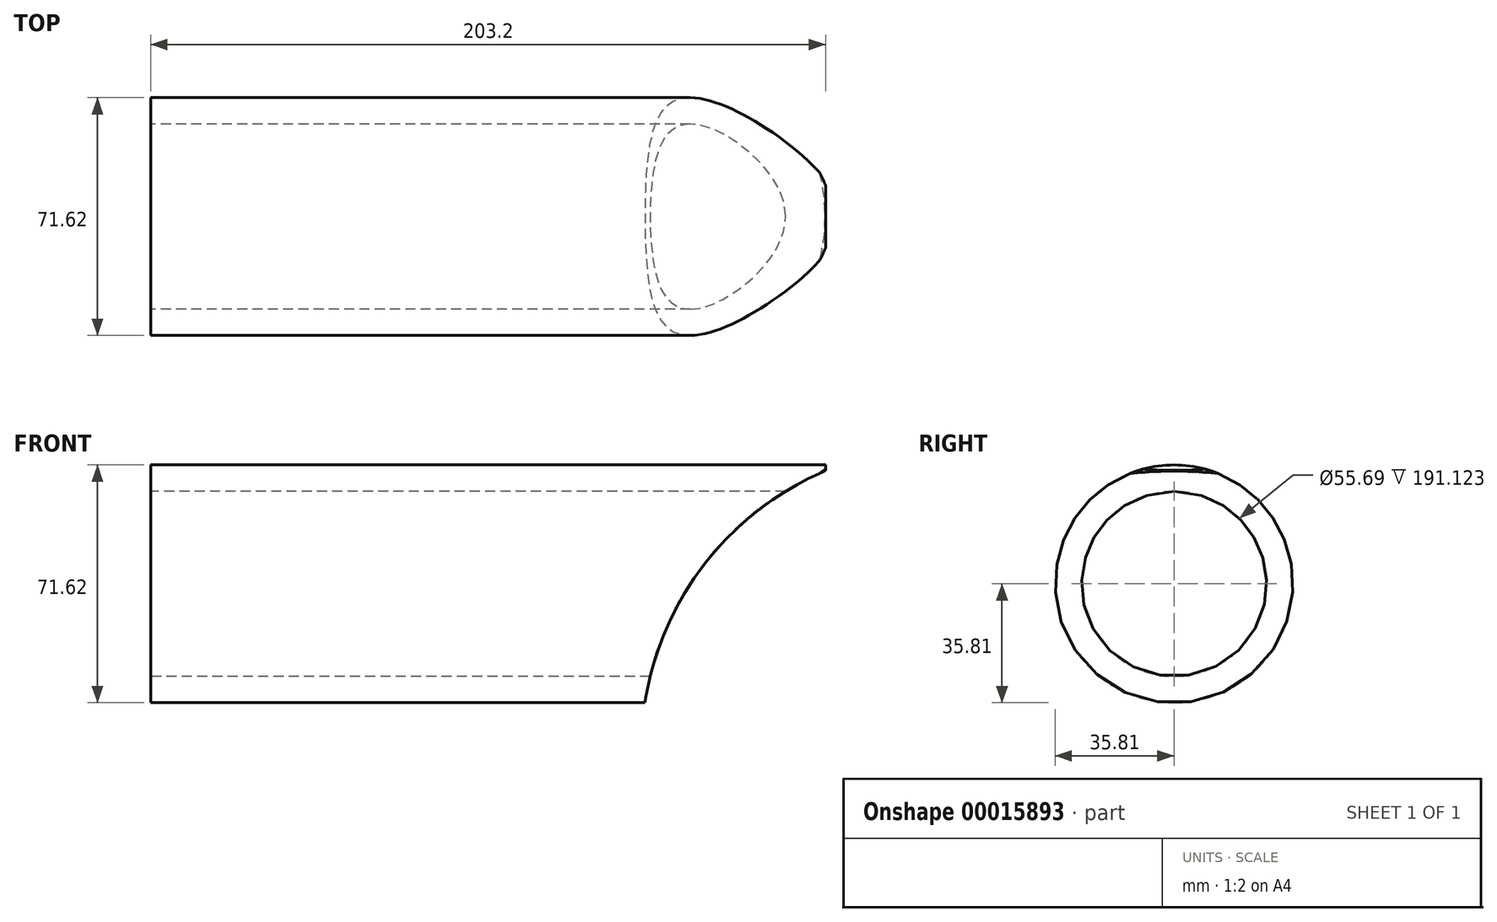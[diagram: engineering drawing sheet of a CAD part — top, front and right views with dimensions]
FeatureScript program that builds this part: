
annotation { "Feature Type Name" : "Feature", "Feature Type Description" : "" }
export const myFeature = defineFeature(function(context is Context, id is Id, definition is map)
    precondition{}
    {
        {
            var Q0;
            Q0=qCreatedBy(makeId("Right.planeOp"),FACE);
            var sketch = newSketch(context, id + "F0", { "sketchPlane" : qUnion([Q0])});
            skCircle(sketch, "E0", {"center": v(0, 0) * mm, "radius": 27.84 * mm});
            skCircle(sketch, "E1", {"center": v(0, 0) * mm, "radius": 35.81 * mm});
            skSolve(sketch);
        }
        {
            var Q0;
            Q0=makeQuery(id+"F0.imprint","IMPRINT",FACE,{"disambiguationData":[TD([[makeQuery(id+"F0.imprint","IMPRINT",EDGE,{"derivedFrom":sQuery(id+"F0.wireOp",EDGE,"E0")}),-1.0]])]});
            extrude(context, id + "F1", {"entities" : qUnion([Q0]), "depth" : 203.2 * mm});
        }
        {
            var Q0;
            Q0=qCreatedBy(makeId("Front.planeOp"),FACE);
            var sketch = newSketch(context, id + "F2", { "sketchPlane" : qUnion([Q0])});
            skCircle(sketch, "E2", {"center": v(238.57, -49.56) * mm, "radius": 90.78 * mm});
            skSolve(sketch);
        }
        {
            var Q0;
            Q0=makeQuery(id+"F2.imprint","IMPRINT",FACE,{"disambiguationData":[TD([[makeQuery(id+"F2.imprint","IMPRINT",EDGE,{"derivedFrom":sQuery(id+"F2.wireOp",EDGE,"E2")}),1.0]])]});
            extrude(context, id + "F3", {"entities" : qUnion([Q0]), "operationType" : NewBodyOperationType.REMOVE, "endBound" : BoundingType.THROUGH_ALL, "oppositeDirection" : true, "depth" : 25.4 * mm, "hasSecondDirection" : true, "secondDirectionBound" : SecondDirectionBoundingType.THROUGH_ALL, "secondDirectionOppositeDirection" : false, "secondDirectionDepth" : 25.4 * mm});
        }
        {
            var Q0;
            Q0=qCreatedBy(makeId("Top.planeOp"),FACE);
            var sketch = newSketch(context, id + "F4", { "sketchPlane" : qUnion([Q0])});
            skLineSegment(sketch, "E3.bottom", {"start": v(166.68, -44.9) * mm, "end": v(182.58, -44.9) * mm});
            skLineSegment(sketch, "E3.top", {"start": v(166.68, -20.7) * mm, "end": v(182.58, -20.7) * mm});
            skLineSegment(sketch, "E3.left", {"start": v(166.68, -44.9) * mm, "end": v(166.68, -20.7) * mm});
            skLineSegment(sketch, "E3.right", {"start": v(182.58, -44.9) * mm, "end": v(182.58, -20.7) * mm});
            skSolve(sketch);
        }
        {
            var Q0;
            Q0=makeQuery(id+"F4.imprint","IMPRINT",FACE,{"disambiguationData":[TD([[makeQuery(id+"F4.imprint","IMPRINT",EDGE,{"derivedFrom":sQuery(id+"F4.wireOp",EDGE,"E3.bottom")}),1.0]])]});
            var Q1;
            Q1=sQuery(id+"F4.wireOp",EDGE,"E3.left");
            var Q2;
            Q2=makeQuery(id+"F3.boolean.opBoolean","INTERSECT",EDGE,{"derivedFrom":[makeQuery(id+"F1.opExtrude","SWEPT_FACE",FACE,{"disambiguationData":[OSD([sQuery(id+"F0.wireOp",EDGE,"E0")])]}),makeQuery(id+"F3.opExtrude","SWEPT_FACE",FACE,{"disambiguationData":[OSD([sQuery(id+"F2.wireOp",EDGE,"E2")])]})]});
            sweep(context, id + "F5", {"operationType" : NewBodyOperationType.REMOVE, "profiles" : qUnion([Q0]), "surfaceProfiles" : qUnion([Q1]), "path" : qUnion([Q2])});
        }
    });
